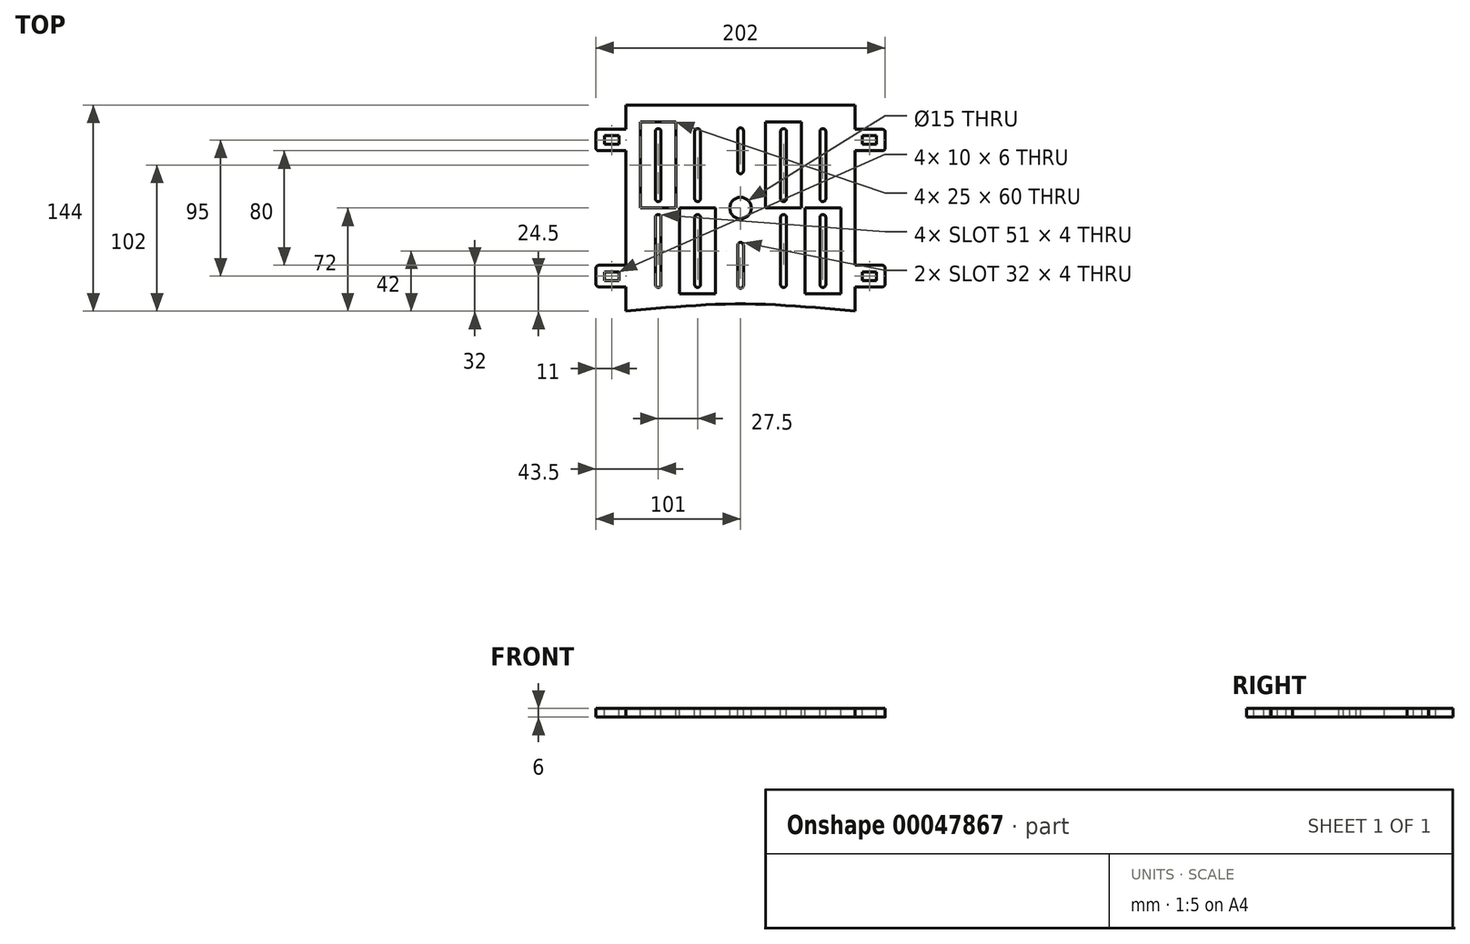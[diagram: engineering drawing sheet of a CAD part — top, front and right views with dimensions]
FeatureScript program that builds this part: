
annotation { "Feature Type Name" : "Feature", "Feature Type Description" : "" }
export const myFeature = defineFeature(function(context is Context, id is Id, definition is map)
    precondition{}
    {
        {
            var Q0;
            Q0=qCreatedBy(makeId("Top.planeOp"),FACE);
            var sketch = newSketch(context, id + "F0", { "sketchPlane" : qUnion([Q0])});
            skCircle(sketch, "E0", {"center": v(0, 0) * mm, "radius": 7.5 * mm});
            skLineSegment(sketch, "E1.rect.bottom", {"start": v(15, -20) * mm, "end": v(-15, -20) * mm});
            skLineSegment(sketch, "E1.rect.top", {"start": v(15, 20) * mm, "end": v(-15, 20) * mm});
            skLineSegment(sketch, "E1.rect.left", {"start": v(15, -20) * mm, "end": v(15, 20) * mm});
            skLineSegment(sketch, "E1.rect.right", {"start": v(-15, -20) * mm, "end": v(-15, 20) * mm});
            skPoint(sketch, "E2.rect.middle", {"position": v(30, -30) * mm});
            skPoint(sketch, "E3.visualSharp", {"position": v(32, -4.5) * mm});
            skLineSegment(sketch, "E2.rect.right", {"start": v(42.5, -60) * mm, "end": v(42.5, 0) * mm});
            skLineSegment(sketch, "E4.rect.top", {"start": v(30, -4.5) * mm, "end": v(30, -4.5) * mm});
            skLineSegment(sketch, "E2.rect.left", {"start": v(17.5, -60) * mm, "end": v(17.5, 0) * mm});
            skPoint(sketch, "E5.visualSharp", {"position": v(28, -55.5) * mm});
            skLineSegment(sketch, "E4.rect.right", {"start": v(28, -53.5) * mm, "end": v(28, -6.5) * mm});
            skPoint(sketch, "E6.visualSharp", {"position": v(32, -55.5) * mm});
            skLineSegment(sketch, "E4.rect.left", {"start": v(32, -53.5) * mm, "end": v(32, -6.5) * mm});
            skPoint(sketch, "E7.visualSharp", {"position": v(28, -4.5) * mm});
            skLineSegment(sketch, "E4.rect.bottom", {"start": v(30, -55.5) * mm, "end": v(30, -55.5) * mm});
            skLineSegment(sketch, "E2.rect.bottom", {"start": v(17.5, -60) * mm, "end": v(42.5, -60) * mm});
            skLineSegment(sketch, "E2.rect.top", {"start": v(17.5, 0) * mm, "end": v(42.5, 0) * mm});
            skArc(sketch, "E6.filletArc", {"start": v(30, -55.5) * mm, "mid": v(31.41, -54.91) * mm, "end": v(32, -53.5) * mm});
            skArc(sketch, "E5.filletArc", {"start": v(28, -53.5) * mm, "mid": v(28.59, -54.91) * mm, "end": v(30, -55.5) * mm});
            skArc(sketch, "E7.filletArc", {"start": v(30, -4.5) * mm, "mid": v(28.59, -5.09) * mm, "end": v(28, -6.5) * mm});
            skArc(sketch, "E3.filletArc", {"start": v(32, -6.5) * mm, "mid": v(31.41, -5.09) * mm, "end": v(30, -4.5) * mm});
            skArc(sketch, "E8.MirrorCS", {"start": v(32, 6.5) * mm, "mid": v(31.41, 5.09) * mm, "end": v(30, 4.5) * mm});
            skArc(sketch, "E9.MirrorCS", {"start": v(30, 4.5) * mm, "mid": v(28.59, 5.09) * mm, "end": v(28, 6.5) * mm});
            skArc(sketch, "E10.MirrorCS", {"start": v(28, 53.5) * mm, "mid": v(28.59, 54.91) * mm, "end": v(30, 55.5) * mm});
            skArc(sketch, "E11.MirrorCS", {"start": v(30, 55.5) * mm, "mid": v(31.41, 54.91) * mm, "end": v(32, 53.5) * mm});
            skPoint(sketch, "E12.MirrorP", {"position": v(32, 4.5) * mm});
            skPoint(sketch, "E13.MirrorP", {"position": v(28, 4.5) * mm});
            skLineSegment(sketch, "E14.MirrorCS", {"start": v(42.5, 60) * mm, "end": v(42.5, 0) * mm});
            skPoint(sketch, "E15.MirrorP", {"position": v(28, 55.5) * mm});
            skLineSegment(sketch, "E16.MirrorCS", {"start": v(17.5, 60) * mm, "end": v(17.5, 0) * mm});
            skPoint(sketch, "E17.MirrorP", {"position": v(32, 55.5) * mm});
            skLineSegment(sketch, "E18.MirrorCS", {"start": v(28, 53.5) * mm, "end": v(28, 6.5) * mm});
            skLineSegment(sketch, "E19.MirrorCS", {"start": v(32, 53.5) * mm, "end": v(32, 6.5) * mm});
            skPoint(sketch, "E20.MirrorP", {"position": v(30, 30) * mm});
            skLineSegment(sketch, "E21.MirrorCS", {"start": v(17.5, 60) * mm, "end": v(42.5, 60) * mm});
            skArc(sketch, "E22.MirrorCS", {"start": v(-30, 55.5) * mm, "mid": v(-31.41, 54.91) * mm, "end": v(-32, 53.5) * mm});
            skArc(sketch, "E23.MirrorCS", {"start": v(-30, 4.5) * mm, "mid": v(-28.59, 5.09) * mm, "end": v(-28, 6.5) * mm});
            skArc(sketch, "E24.MirrorCS", {"start": v(-30, -4.5) * mm, "mid": v(-28.59, -5.09) * mm, "end": v(-28, -6.5) * mm});
            skArc(sketch, "E25.MirrorCS", {"start": v(-28, 53.5) * mm, "mid": v(-28.59, 54.91) * mm, "end": v(-30, 55.5) * mm});
            skArc(sketch, "E26.MirrorCS", {"start": v(-30, -55.5) * mm, "mid": v(-31.41, -54.91) * mm, "end": v(-32, -53.5) * mm});
            skArc(sketch, "E27.MirrorCS", {"start": v(-32, -6.5) * mm, "mid": v(-31.41, -5.09) * mm, "end": v(-30, -4.5) * mm});
            skArc(sketch, "E28.MirrorCS", {"start": v(-32, 6.5) * mm, "mid": v(-31.41, 5.09) * mm, "end": v(-30, 4.5) * mm});
            skArc(sketch, "E29.MirrorCS", {"start": v(-28, -53.5) * mm, "mid": v(-28.59, -54.91) * mm, "end": v(-30, -55.5) * mm});
            skLineSegment(sketch, "E30.MirrorCS", {"start": v(-17.5, 0) * mm, "end": v(-42.5, 0) * mm});
            skPoint(sketch, "E31.MirrorP", {"position": v(-28, 55.5) * mm});
            skPoint(sketch, "E32.MirrorP", {"position": v(-32, -55.5) * mm});
            skPoint(sketch, "E33.MirrorP", {"position": v(-32, 4.5) * mm});
            skPoint(sketch, "E34.MirrorP", {"position": v(-30, 30) * mm});
            skPoint(sketch, "E35.MirrorP", {"position": v(-30, -30) * mm});
            skLineSegment(sketch, "E36.MirrorCS", {"start": v(-28, 53.5) * mm, "end": v(-28, 6.5) * mm});
            skLineSegment(sketch, "E37.MirrorCS", {"start": v(-17.5, 60) * mm, "end": v(-42.5, 60) * mm});
            skPoint(sketch, "E38.MirrorP", {"position": v(-28, -55.5) * mm});
            skLineSegment(sketch, "E39.MirrorCS", {"start": v(-42.5, 60) * mm, "end": v(-42.5, 0) * mm});
            skLineSegment(sketch, "E40.MirrorCS", {"start": v(-42.5, -60) * mm, "end": v(-42.5, 0) * mm});
            skPoint(sketch, "E41.MirrorP", {"position": v(-32, 55.5) * mm});
            skLineSegment(sketch, "E42.MirrorCS", {"start": v(-32, -53.5) * mm, "end": v(-32, -6.5) * mm});
            skLineSegment(sketch, "E43.MirrorCS", {"start": v(-17.5, -60) * mm, "end": v(-42.5, -60) * mm});
            skPoint(sketch, "E44.MirrorP", {"position": v(-32, -4.5) * mm});
            skLineSegment(sketch, "E45.MirrorCS", {"start": v(-28, -53.5) * mm, "end": v(-28, -6.5) * mm});
            skPoint(sketch, "E46.MirrorP", {"position": v(-28, -4.5) * mm});
            skLineSegment(sketch, "E47.MirrorCS", {"start": v(-17.5, 60) * mm, "end": v(-17.5, 0) * mm});
            skPoint(sketch, "E48.MirrorP", {"position": v(-28, 4.5) * mm});
            skLineSegment(sketch, "E49.MirrorCS", {"start": v(-17.5, -60) * mm, "end": v(-17.5, 0) * mm});
            skLineSegment(sketch, "E50.MirrorCS", {"start": v(-32, 53.5) * mm, "end": v(-32, 6.5) * mm});
            skLineSegment(sketch, "E51.bottom", {"start": v(-15, 60) * mm, "end": v(15, 60) * mm});
            skLineSegment(sketch, "E51.top", {"start": v(-15, 20) * mm, "end": v(15, 20) * mm});
            skLineSegment(sketch, "E51.left", {"start": v(-15, 60) * mm, "end": v(-15, 20) * mm});
            skLineSegment(sketch, "E51.right", {"start": v(15, 60) * mm, "end": v(15, 20) * mm});
            skLineSegment(sketch, "E52.rect.bottom", {"start": v(0, 24) * mm, "end": v(0, 24) * mm});
            skLineSegment(sketch, "E52.rect.top", {"start": v(0, 56) * mm, "end": v(0, 56) * mm});
            skLineSegment(sketch, "E52.rect.left", {"start": v(2, 26) * mm, "end": v(2, 54) * mm});
            skLineSegment(sketch, "E52.rect.right", {"start": v(-2, 26) * mm, "end": v(-2, 54) * mm});
            skPoint(sketch, "E52.rect.middle", {"position": v(0, 40) * mm});
            skPoint(sketch, "E52.rect.middle.positionSnap0", {"position": v(15, 40) * mm});
            skPoint(sketch, "E52.rect.centerSnap0", {"position": v(15, 40) * mm});
            skLineSegment(sketch, "E53.MirrorCS", {"start": v(0, -24) * mm, "end": v(0, -24) * mm});
            skLineSegment(sketch, "E54.MirrorCS", {"start": v(0, -56) * mm, "end": v(0, -56) * mm});
            skPoint(sketch, "E55.MirrorP", {"position": v(15, -40) * mm});
            skLineSegment(sketch, "E56.MirrorCS", {"start": v(15, -60) * mm, "end": v(15, -20) * mm});
            skPoint(sketch, "E57.MirrorP", {"position": v(0, -40) * mm});
            skLineSegment(sketch, "E58.MirrorCS", {"start": v(-15, -60) * mm, "end": v(15, -60) * mm});
            skLineSegment(sketch, "E59.MirrorCS", {"start": v(-15, -20) * mm, "end": v(15, -20) * mm});
            skLineSegment(sketch, "E60.MirrorCS", {"start": v(2, -26) * mm, "end": v(2, -54) * mm});
            skLineSegment(sketch, "E61.MirrorCS", {"start": v(-2, -26) * mm, "end": v(-2, -54) * mm});
            skLineSegment(sketch, "E62.MirrorCS", {"start": v(-15, -60) * mm, "end": v(-15, -20) * mm});
            skLineSegment(sketch, "E63", {"start": v(43.75, 61.97) * mm, "end": v(43.75, -67.11) * mm, "construction": true});
            skArc(sketch, "E64.MirrorCS", {"start": v(57.5, -55.5) * mm, "mid": v(56.09, -54.91) * mm, "end": v(55.5, -53.5) * mm});
            skArc(sketch, "E65.MirrorCS", {"start": v(55.5, -6.5) * mm, "mid": v(56.09, -5.09) * mm, "end": v(57.5, -4.5) * mm});
            skArc(sketch, "E66.MirrorCS", {"start": v(57.5, -4.5) * mm, "mid": v(58.91, -5.09) * mm, "end": v(59.5, -6.5) * mm});
            skArc(sketch, "E67.MirrorCS", {"start": v(59.5, -53.5) * mm, "mid": v(58.91, -54.91) * mm, "end": v(57.5, -55.5) * mm});
            skArc(sketch, "E68.MirrorCS", {"start": v(57.5, 4.5) * mm, "mid": v(58.91, 5.09) * mm, "end": v(59.5, 6.5) * mm});
            skArc(sketch, "E69.MirrorCS", {"start": v(59.5, 53.5) * mm, "mid": v(58.91, 54.91) * mm, "end": v(57.5, 55.5) * mm});
            skArc(sketch, "E70.MirrorCS", {"start": v(57.5, 55.5) * mm, "mid": v(56.09, 54.91) * mm, "end": v(55.5, 53.5) * mm});
            skArc(sketch, "E71.MirrorCS", {"start": v(55.5, 6.5) * mm, "mid": v(56.09, 5.09) * mm, "end": v(57.5, 4.5) * mm});
            skPoint(sketch, "E72.MirrorP", {"position": v(59.5, 55.5) * mm});
            skPoint(sketch, "E73.MirrorP", {"position": v(55.5, 4.5) * mm});
            skLineSegment(sketch, "E74.MirrorCS", {"start": v(70, 60) * mm, "end": v(45, 60) * mm});
            skLineSegment(sketch, "E75.MirrorCS", {"start": v(70, 0) * mm, "end": v(45, 0) * mm});
            skLineSegment(sketch, "E76.MirrorCS", {"start": v(70, -60) * mm, "end": v(45, -60) * mm});
            skLineSegment(sketch, "E77.MirrorCS", {"start": v(55.5, -53.5) * mm, "end": v(55.5, -6.5) * mm});
            skLineSegment(sketch, "E78.MirrorCS", {"start": v(45, -60) * mm, "end": v(45, 0) * mm});
            skPoint(sketch, "E79.MirrorP", {"position": v(59.5, 4.5) * mm});
            skLineSegment(sketch, "E80.MirrorCS", {"start": v(55.5, 53.5) * mm, "end": v(55.5, 6.5) * mm});
            skPoint(sketch, "E81.MirrorP", {"position": v(55.5, -55.5) * mm});
            skPoint(sketch, "E82.MirrorP", {"position": v(59.5, -4.5) * mm});
            skPoint(sketch, "E83.MirrorP", {"position": v(57.5, -30) * mm});
            skPoint(sketch, "E84.MirrorP", {"position": v(55.5, 55.5) * mm});
            skLineSegment(sketch, "E85.MirrorCS", {"start": v(59.5, 53.5) * mm, "end": v(59.5, 6.5) * mm});
            skPoint(sketch, "E86.MirrorP", {"position": v(59.5, -55.5) * mm});
            skLineSegment(sketch, "E87.MirrorCS", {"start": v(70, 60) * mm, "end": v(70, 0) * mm});
            skPoint(sketch, "E88.MirrorP", {"position": v(57.5, 30) * mm});
            skLineSegment(sketch, "E89.MirrorCS", {"start": v(59.5, -53.5) * mm, "end": v(59.5, -6.5) * mm});
            skPoint(sketch, "E90.MirrorP", {"position": v(55.5, -4.5) * mm});
            skLineSegment(sketch, "E91.MirrorCS", {"start": v(45, 60) * mm, "end": v(45, 0) * mm});
            skLineSegment(sketch, "E92.MirrorCS", {"start": v(70, -60) * mm, "end": v(70, 0) * mm});
            skArc(sketch, "E93.MirrorCS", {"start": v(-57.5, -55.5) * mm, "mid": v(-56.09, -54.91) * mm, "end": v(-55.5, -53.5) * mm});
            skArc(sketch, "E94.MirrorCS", {"start": v(-59.5, 53.5) * mm, "mid": v(-58.91, 54.91) * mm, "end": v(-57.5, 55.5) * mm});
            skArc(sketch, "E95.MirrorCS", {"start": v(-59.5, -53.5) * mm, "mid": v(-58.91, -54.91) * mm, "end": v(-57.5, -55.5) * mm});
            skArc(sketch, "E96.MirrorCS", {"start": v(-57.5, 55.5) * mm, "mid": v(-56.09, 54.91) * mm, "end": v(-55.5, 53.5) * mm});
            skArc(sketch, "E97.MirrorCS", {"start": v(-57.5, 4.5) * mm, "mid": v(-58.91, 5.09) * mm, "end": v(-59.5, 6.5) * mm});
            skArc(sketch, "E98.MirrorCS", {"start": v(-55.5, 6.5) * mm, "mid": v(-56.09, 5.09) * mm, "end": v(-57.5, 4.5) * mm});
            skArc(sketch, "E99.MirrorCS", {"start": v(-57.5, -4.5) * mm, "mid": v(-58.91, -5.09) * mm, "end": v(-59.5, -6.5) * mm});
            skArc(sketch, "E100.MirrorCS", {"start": v(-55.5, -6.5) * mm, "mid": v(-56.09, -5.09) * mm, "end": v(-57.5, -4.5) * mm});
            skLineSegment(sketch, "E101.MirrorCS", {"start": v(-55.5, -53.5) * mm, "end": v(-55.5, -6.5) * mm});
            skLineSegment(sketch, "E102.MirrorCS", {"start": v(-70, 60) * mm, "end": v(-70, 0) * mm});
            skLineSegment(sketch, "E103.MirrorCS", {"start": v(-59.5, 53.5) * mm, "end": v(-59.5, 6.5) * mm});
            skPoint(sketch, "E104.MirrorP", {"position": v(-57.5, -30) * mm});
            skPoint(sketch, "E105.MirrorP", {"position": v(-57.5, 30) * mm});
            skLineSegment(sketch, "E106.MirrorCS", {"start": v(-45, -60) * mm, "end": v(-45, 0) * mm});
            skPoint(sketch, "E107.MirrorP", {"position": v(-55.5, -55.5) * mm});
            skLineSegment(sketch, "E108.MirrorCS", {"start": v(-70, -60) * mm, "end": v(-45, -60) * mm});
            skPoint(sketch, "E109.MirrorP", {"position": v(-59.5, 4.5) * mm});
            skLineSegment(sketch, "E110.MirrorCS", {"start": v(-70, 0) * mm, "end": v(-45, 0) * mm});
            skPoint(sketch, "E111.MirrorP", {"position": v(-59.5, -4.5) * mm});
            skLineSegment(sketch, "E112.MirrorCS", {"start": v(-45, 60) * mm, "end": v(-45, 0) * mm});
            skLineSegment(sketch, "E113.MirrorCS", {"start": v(-55.5, 53.5) * mm, "end": v(-55.5, 6.5) * mm});
            skPoint(sketch, "E114.MirrorP", {"position": v(-59.5, -55.5) * mm});
            skLineSegment(sketch, "E115.MirrorCS", {"start": v(-70, -60) * mm, "end": v(-70, 0) * mm});
            skLineSegment(sketch, "E116.MirrorCS", {"start": v(-70, 60) * mm, "end": v(-45, 60) * mm});
            skLineSegment(sketch, "E117.MirrorCS", {"start": v(-59.5, -53.5) * mm, "end": v(-59.5, -6.5) * mm});
            skPoint(sketch, "E118.MirrorP", {"position": v(-55.5, -4.5) * mm});
            skPoint(sketch, "E119.MirrorP", {"position": v(-55.5, 55.5) * mm});
            skPoint(sketch, "E120.MirrorP", {"position": v(-55.5, 4.5) * mm});
            skPoint(sketch, "E121.MirrorP", {"position": v(-59.5, 55.5) * mm});
            skLineSegment(sketch, "E122.rect.bottom", {"start": v(80, -72) * mm, "end": v(-80, -72) * mm, "construction": true});
            skLineSegment(sketch, "E122.rect.top", {"start": v(80, 72) * mm, "end": v(-80, 72) * mm, "construction": true});
            skLineSegment(sketch, "E122.rect.left", {"start": v(80, -72) * mm, "end": v(80, 72) * mm, "construction": true});
            skLineSegment(sketch, "E122.rect.right", {"start": v(-80, -72) * mm, "end": v(-80, 72) * mm, "construction": true});
            skPoint(sketch, "E123.endSnap0", {"position": v(0, 72) * mm});
            skLineSegment(sketch, "E124", {"start": v(0, -72) * mm, "end": v(0, -67) * mm, "construction": true});
            skFitSpline(sketch, "E125", {"points": [v(-80, -72) * mm, v(0, -67) * mm, v(80, -72) * mm], "startDerivative": vector(160, 15) * mm, "endDerivative": vector(160, -15) * mm, "construction": true});
            skPoint(sketch, "E126.visualSharp", {"position": v(-2, 24) * mm});
            skArc(sketch, "E126.filletArc", {"start": v(-2, 26) * mm, "mid": v(-1.41, 24.59) * mm, "end": v(0, 24) * mm});
            skPoint(sketch, "E127.visualSharp", {"position": v(-2, 56) * mm});
            skArc(sketch, "E127.filletArc", {"start": v(0, 56) * mm, "mid": v(-1.41, 55.41) * mm, "end": v(-2, 54) * mm});
            skPoint(sketch, "E128.visualSharp", {"position": v(2, 24) * mm});
            skArc(sketch, "E128.filletArc", {"start": v(0, 24) * mm, "mid": v(1.41, 24.59) * mm, "end": v(2, 26) * mm});
            skPoint(sketch, "E129.visualSharp", {"position": v(2, 56) * mm});
            skArc(sketch, "E129.filletArc", {"start": v(2, 54) * mm, "mid": v(1.41, 55.41) * mm, "end": v(0, 56) * mm});
            skPoint(sketch, "E130.visualSharp", {"position": v(-2, -24) * mm});
            skArc(sketch, "E130.filletArc", {"start": v(0, -24) * mm, "mid": v(-1.41, -24.59) * mm, "end": v(-2, -26) * mm});
            skPoint(sketch, "E131.visualSharp", {"position": v(-2, -56) * mm});
            skArc(sketch, "E131.filletArc", {"start": v(-2, -54) * mm, "mid": v(-1.41, -55.41) * mm, "end": v(0, -56) * mm});
            skPoint(sketch, "E132.visualSharp", {"position": v(2, -56) * mm});
            skArc(sketch, "E132.filletArc", {"start": v(0, -56) * mm, "mid": v(1.41, -55.41) * mm, "end": v(2, -54) * mm});
            skPoint(sketch, "E133.visualSharp", {"position": v(2, -24) * mm});
            skArc(sketch, "E133.filletArc", {"start": v(2, -26) * mm, "mid": v(1.41, -24.59) * mm, "end": v(0, -24) * mm});
            skSolve(sketch);
        }
        {
            var Q0;
            Q0=qCreatedBy(makeId("Top.planeOp"),FACE);
            var sketch = newSketch(context, id + "F1", { "sketchPlane" : qUnion([Q0])});
            skLineSegment(sketch, "E134.rect.bottom", {"start": v(80, -72) * mm, "end": v(-80, -72) * mm});
            skLineSegment(sketch, "E134.rect.top", {"start": v(80, 72) * mm, "end": v(-80, 72) * mm});
            skLineSegment(sketch, "E134.rect.left", {"start": v(80, -72) * mm, "end": v(80, 72) * mm});
            skLineSegment(sketch, "E134.rect.right", {"start": v(-80, -72) * mm, "end": v(-80, 72) * mm});
            skPoint(sketch, "E134.rect.middle", {"position": v(0, 0) * mm});
            skLineSegment(sketch, "E135", {"start": v(-80, 0) * mm, "end": v(-91.26, 0) * mm, "construction": true});
            skPoint(sketch, "E135.endSnap0", {"position": v(-80, 0) * mm});
            skLineSegment(sketch, "E136.bottom", {"start": v(-101, 55) * mm, "end": v(-80, 55) * mm});
            skLineSegment(sketch, "E136.top", {"start": v(-101, 40) * mm, "end": v(-80, 40) * mm});
            skLineSegment(sketch, "E136.left", {"start": v(-101, 55) * mm, "end": v(-101, 40) * mm});
            skLineSegment(sketch, "E136.right", {"start": v(-80, 55) * mm, "end": v(-80, 40) * mm});
            skLineSegment(sketch, "E137.MirrorCS", {"start": v(101, 40) * mm, "end": v(80, 40) * mm});
            skLineSegment(sketch, "E138.MirrorCS", {"start": v(101, 55) * mm, "end": v(101, 40) * mm});
            skLineSegment(sketch, "E139.MirrorCS", {"start": v(101, 55) * mm, "end": v(80, 55) * mm});
            skLineSegment(sketch, "E140.MirrorCS", {"start": v(-101, -40) * mm, "end": v(-80, -40) * mm});
            skLineSegment(sketch, "E141.MirrorCS", {"start": v(-101, -55) * mm, "end": v(-101, -40) * mm});
            skLineSegment(sketch, "E142.MirrorCS", {"start": v(-101, -55) * mm, "end": v(-80, -55) * mm});
            skLineSegment(sketch, "E143.MirrorCS", {"start": v(101, -40) * mm, "end": v(80, -40) * mm});
            skLineSegment(sketch, "E144.MirrorCS", {"start": v(101, -55) * mm, "end": v(101, -40) * mm});
            skLineSegment(sketch, "E145.MirrorCS", {"start": v(101, -55) * mm, "end": v(80, -55) * mm});
            skSolve(sketch);
        }
        {
            var Q0;
            Q0 = qSketchRegion(id + "F1", true);
            extrude(context, id + "F2", {"entities" : qUnion([Q0]), "oppositeDirection" : true, "depth" : 6 * mm});
        }
        {
            var Q0;
            Q0=makeQuery(id+"F0.imprint","IMPRINT",FACE,{"disambiguationData":[TD([[makeQuery(id+"F0.imprint","IMPRINT",EDGE,{"derivedFrom":sQuery(id+"F0.wireOp",EDGE,"E94.MirrorCS")}),-1.0]])]});
            var Q1;
            Q1=makeQuery(id+"F0.imprint","IMPRINT",FACE,{"disambiguationData":[TD([[makeQuery(id+"F0.imprint","IMPRINT",EDGE,{"derivedFrom":sQuery(id+"F0.wireOp",EDGE,"E93.MirrorCS")}),1.0]])]});
            var Q2;
            Q2=makeQuery(id+"F0.imprint","IMPRINT",FACE,{"disambiguationData":[TD([[makeQuery(id+"F0.imprint","IMPRINT",EDGE,{"derivedFrom":sQuery(id+"F0.wireOp",EDGE,"E22.MirrorCS")}),1.0]])]});
            var Q3;
            Q3=makeQuery(id+"F0.imprint","IMPRINT",FACE,{"disambiguationData":[TD([[makeQuery(id+"F0.imprint","IMPRINT",EDGE,{"derivedFrom":sQuery(id+"F0.wireOp",EDGE,"E24.MirrorCS")}),-1.0]])]});
            var Q4;
            Q4=makeQuery(id+"F0.imprint","IMPRINT",FACE,{"disambiguationData":[TD([[makeQuery(id+"F0.imprint","IMPRINT",EDGE,{"derivedFrom":sQuery(id+"F0.wireOp",EDGE,"E0")}),1.0]])]});
            var Q5;
            Q5=makeQuery(id+"F0.imprint","IMPRINT",FACE,{"disambiguationData":[TD([[makeQuery(id+"F0.imprint","IMPRINT",EDGE,{"derivedFrom":sQuery(id+"F0.wireOp",EDGE,"E52.rect.left")}),1.0]])]});
            var Q6;
            Q6=makeQuery(id+"F0.imprint","IMPRINT",FACE,{"disambiguationData":[TD([[makeQuery(id+"F0.imprint","IMPRINT",EDGE,{"derivedFrom":sQuery(id+"F0.wireOp",EDGE,"E60.MirrorCS")}),-1.0]])]});
            var Q7;
            Q7=makeQuery(id+"F0.imprint","IMPRINT",FACE,{"disambiguationData":[TD([[makeQuery(id+"F0.imprint","IMPRINT",EDGE,{"derivedFrom":sQuery(id+"F0.wireOp",EDGE,"E4.rect.right")}),-1.0]])]});
            var Q8;
            Q8=makeQuery(id+"F0.imprint","IMPRINT",FACE,{"disambiguationData":[TD([[makeQuery(id+"F0.imprint","IMPRINT",EDGE,{"derivedFrom":sQuery(id+"F0.wireOp",EDGE,"E8.MirrorCS")}),-1.0]])]});
            var Q9;
            Q9=makeQuery(id+"F0.imprint","IMPRINT",FACE,{"disambiguationData":[TD([[makeQuery(id+"F0.imprint","IMPRINT",EDGE,{"derivedFrom":sQuery(id+"F0.wireOp",EDGE,"E68.MirrorCS")}),1.0]])]});
            var Q10;
            Q10=makeQuery(id+"F0.imprint","IMPRINT",FACE,{"disambiguationData":[TD([[makeQuery(id+"F0.imprint","IMPRINT",EDGE,{"derivedFrom":sQuery(id+"F0.wireOp",EDGE,"E64.MirrorCS")}),-1.0]])]});
            extrude(context, id + "F3", {"entities" : qUnion([Q0, Q1, Q2, Q3, Q4, Q5, Q6, Q7, Q8, Q9, Q10]), "operationType" : NewBodyOperationType.REMOVE, "oppositeDirection" : true, "depth" : 25 * mm});
        }
        {
            var Q0;
            Q0=makeQuery(id+"F2.opExtrude","CAP_FACE",FACE,{"disambiguationData":[OSD([sQuery(id+"F1.wireOp",EDGE,"E134.rect.bottom"),sQuery(id+"F1.wireOp",EDGE,"E134.rect.top"),sQuery(id+"F1.wireOp",EDGE,"E134.rect.left"),sQuery(id+"F1.wireOp",EDGE,"E134.rect.right")])],"isStart":true});
            var sketch = newSketch(context, id + "F4", { "sketchPlane" : qUnion([Q0])});
            skFitSpline(sketch, "E146", {"points": [v(-80, -72) * mm, v(0, -66.98) * mm, v(80, -72) * mm], "startDerivative": vector(160, 15.06) * mm, "endDerivative": vector(160, -15.06) * mm});
            skLineSegment(sketch, "E147", {"start": v(-80, -72) * mm, "end": v(-75.68, -86.1) * mm});
            skLineSegment(sketch, "E148", {"start": v(-75.68, -86.1) * mm, "end": v(77.36, -86.1) * mm});
            skLineSegment(sketch, "E149", {"start": v(77.36, -86.1) * mm, "end": v(80, -72) * mm});
            skSolve(sketch);
        }
        {
            var Q0;
            Q0 = qSketchRegion(id + "F4", true);
            extrude(context, id + "F5", {"entities" : qUnion([Q0]), "operationType" : NewBodyOperationType.REMOVE, "oppositeDirection" : true, "depth" : 25 * mm});
        }
        {
            var Q0;
            Q0=makeQuery(id+"F2.opExtrude","SWEPT_EDGE",EDGE,{"disambiguationData":[OSD([sQuery(id+"F1.wireOp",EDGE,"E136.top"),sQuery(id+"F1.wireOp",EDGE,"E136.left")])]});
            var Q1;
            Q1=makeQuery(id+"F2.opExtrude","SWEPT_EDGE",EDGE,{"disambiguationData":[OSD([sQuery(id+"F1.wireOp",EDGE,"E136.bottom"),sQuery(id+"F1.wireOp",EDGE,"E136.left")])]});
            var Q2;
            Q2=makeQuery(id+"F2.opExtrude","SWEPT_EDGE",EDGE,{"disambiguationData":[OSD([sQuery(id+"F1.wireOp",EDGE,"E140.MirrorCS"),sQuery(id+"F1.wireOp",EDGE,"E141.MirrorCS")])]});
            var Q3;
            Q3=makeQuery(id+"F2.opExtrude","SWEPT_EDGE",EDGE,{"disambiguationData":[OSD([sQuery(id+"F1.wireOp",EDGE,"E141.MirrorCS"),sQuery(id+"F1.wireOp",EDGE,"E142.MirrorCS")])]});
            var Q4;
            Q4=makeQuery(id+"F2.opExtrude","SWEPT_EDGE",EDGE,{"disambiguationData":[OSD([sQuery(id+"F1.wireOp",EDGE,"E144.MirrorCS"),sQuery(id+"F1.wireOp",EDGE,"E145.MirrorCS")])]});
            var Q5;
            Q5=makeQuery(id+"F2.opExtrude","SWEPT_EDGE",EDGE,{"disambiguationData":[OSD([sQuery(id+"F1.wireOp",EDGE,"E143.MirrorCS"),sQuery(id+"F1.wireOp",EDGE,"E144.MirrorCS")])]});
            var Q6;
            Q6=makeQuery(id+"F2.opExtrude","SWEPT_EDGE",EDGE,{"disambiguationData":[OSD([sQuery(id+"F1.wireOp",EDGE,"E137.MirrorCS"),sQuery(id+"F1.wireOp",EDGE,"E138.MirrorCS")])]});
            var Q7;
            Q7=makeQuery(id+"F2.opExtrude","SWEPT_EDGE",EDGE,{"disambiguationData":[OSD([sQuery(id+"F1.wireOp",EDGE,"E138.MirrorCS"),sQuery(id+"F1.wireOp",EDGE,"E139.MirrorCS")])]});
            fillet(context, id + "F6", {"entities" : qUnion([Q0, Q1, Q2, Q3, Q4, Q5, Q6, Q7]), "radius" : 2 * mm, "tangentPropagation" : true, "allowEdgeOverflow" : false});
        }
        {
            var Q0;
            Q0=makeQuery(id+"F1.imprint","IMPRINT",FACE,{"disambiguationData":[TD([[makeQuery(id+"F1.imprint","IMPRINT",EDGE,{"derivedFrom":sQuery(id+"F1.wireOp",EDGE,"E136.bottom")}),-1.0]])]});
            var sketch = newSketch(context, id + "F7", { "sketchPlane" : qUnion([Q0])});
            skLineSegment(sketch, "E150", {"start": v(-101, 47.5) * mm, "end": v(-79, 47.5) * mm, "construction": true});
            skLineSegment(sketch, "E151.rect.bottom", {"start": v(-85, 50.5) * mm, "end": v(-95, 50.5) * mm});
            skLineSegment(sketch, "E151.rect.top", {"start": v(-85, 44.5) * mm, "end": v(-95, 44.5) * mm});
            skLineSegment(sketch, "E151.rect.left", {"start": v(-85, 50.5) * mm, "end": v(-85, 44.5) * mm});
            skLineSegment(sketch, "E151.rect.right", {"start": v(-95, 50.5) * mm, "end": v(-95, 44.5) * mm});
            skPoint(sketch, "E151.rect.middle", {"position": v(-90, 47.5) * mm});
            skLineSegment(sketch, "E152.MirrorCS", {"start": v(-85, -44.5) * mm, "end": v(-95, -44.5) * mm});
            skLineSegment(sketch, "E153.MirrorCS", {"start": v(-95, -50.5) * mm, "end": v(-95, -44.5) * mm});
            skLineSegment(sketch, "E154.MirrorCS", {"start": v(-85, -50.5) * mm, "end": v(-95, -50.5) * mm});
            skLineSegment(sketch, "E155.MirrorCS", {"start": v(-85, -50.5) * mm, "end": v(-85, -44.5) * mm});
            skLineSegment(sketch, "E156.MirrorCS", {"start": v(85, 50.5) * mm, "end": v(95, 50.5) * mm});
            skLineSegment(sketch, "E157.MirrorCS", {"start": v(101, 47.5) * mm, "end": v(79, 47.5) * mm, "construction": true});
            skLineSegment(sketch, "E158.MirrorCS", {"start": v(95, 50.5) * mm, "end": v(95, 44.5) * mm});
            skLineSegment(sketch, "E159.MirrorCS", {"start": v(85, 44.5) * mm, "end": v(95, 44.5) * mm});
            skLineSegment(sketch, "E160.MirrorCS", {"start": v(85, 50.5) * mm, "end": v(85, 44.5) * mm});
            skLineSegment(sketch, "E161.MirrorCS", {"start": v(85, -44.5) * mm, "end": v(95, -44.5) * mm});
            skLineSegment(sketch, "E162.MirrorCS", {"start": v(95, -50.5) * mm, "end": v(95, -44.5) * mm});
            skLineSegment(sketch, "E163.MirrorCS", {"start": v(85, -50.5) * mm, "end": v(95, -50.5) * mm});
            skLineSegment(sketch, "E164.MirrorCS", {"start": v(85, -50.5) * mm, "end": v(85, -44.5) * mm});
            skSolve(sketch);
        }
        {
            var Q0;
            Q0 = qSketchRegion(id + "F7", true);
            extrude(context, id + "F8", {"entities" : qUnion([Q0]), "operationType" : NewBodyOperationType.REMOVE, "oppositeDirection" : true, "depth" : 25 * mm});
        }
    });
